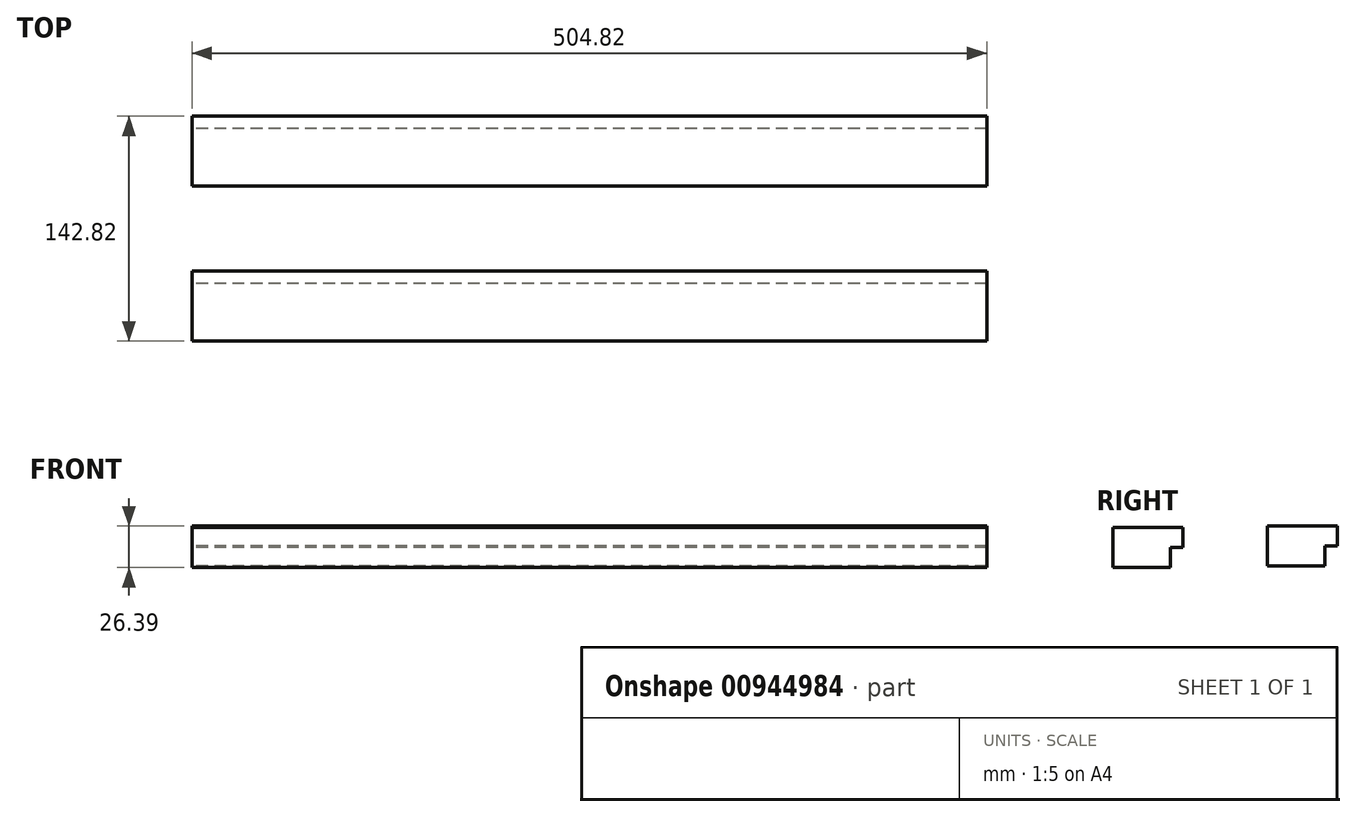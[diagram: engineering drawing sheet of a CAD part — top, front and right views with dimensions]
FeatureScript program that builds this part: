
annotation { "Feature Type Name" : "Feature", "Feature Type Description" : "" }
export const myFeature = defineFeature(function(context is Context, id is Id, definition is map)
    precondition{}
    {
        {
            var Q0;
            Q0=qCreatedBy(makeId("Right.planeOp"),FACE);
            var sketch = newSketch(context, id + "F0", { "sketchPlane" : qUnion([Q0])});
            skLineSegment(sketch, "E0.bottom", {"start": v(-98.37, 30.25) * mm, "end": v(-61.85, 30.25) * mm});
            skLineSegment(sketch, "E0.top", {"start": v(-98.37, 4.85) * mm, "end": v(-61.85, 4.85) * mm});
            skLineSegment(sketch, "E0.left", {"start": v(-98.37, 30.25) * mm, "end": v(-98.37, 4.85) * mm});
            skLineSegment(sketch, "E0.right", {"start": v(-61.85, 30.25) * mm, "end": v(-61.85, 4.85) * mm});
            skLineSegment(sketch, "E1.bottom", {"start": v(-61.85, 30.25) * mm, "end": v(-53.92, 30.25) * mm});
            skLineSegment(sketch, "E1.top", {"start": v(-61.85, 17.55) * mm, "end": v(-53.92, 17.55) * mm});
            skLineSegment(sketch, "E1.left", {"start": v(-61.85, 30.25) * mm, "end": v(-61.85, 17.55) * mm});
            skLineSegment(sketch, "E1.right", {"start": v(-53.92, 30.25) * mm, "end": v(-53.92, 17.55) * mm});
            skLineSegment(sketch, "E2.bottom", {"start": v(0, 31.24) * mm, "end": v(36.51, 31.24) * mm});
            skLineSegment(sketch, "E2.top", {"start": v(0, 5.84) * mm, "end": v(36.51, 5.84) * mm});
            skLineSegment(sketch, "E2.left", {"start": v(0, 31.24) * mm, "end": v(0, 5.84) * mm});
            skLineSegment(sketch, "E2.right", {"start": v(36.51, 31.24) * mm, "end": v(36.51, 5.84) * mm});
            skLineSegment(sketch, "E3.bottom", {"start": v(36.51, 31.24) * mm, "end": v(44.45, 31.24) * mm});
            skLineSegment(sketch, "E3.top", {"start": v(36.51, 18.54) * mm, "end": v(44.45, 18.54) * mm});
            skLineSegment(sketch, "E3.left", {"start": v(36.51, 31.24) * mm, "end": v(36.51, 18.54) * mm});
            skLineSegment(sketch, "E3.right", {"start": v(44.45, 31.24) * mm, "end": v(44.45, 18.54) * mm});
            skSolve(sketch);
        }
        {
            var Q0;
            Q0=makeQuery(id+"F0.imprint","IMPRINT",FACE,{"disambiguationData":[TD([[makeQuery(id+"F0.imprint","IMPRINT",EDGE,{"derivedFrom":sQuery(id+"F0.wireOp",EDGE,"E0.bottom")}),-1.0]])]});
            var Q1;
            Q1=makeQuery(id+"F0.imprint","IMPRINT",FACE,{"disambiguationData":[TD([[makeQuery(id+"F0.imprint","IMPRINT",EDGE,{"derivedFrom":sQuery(id+"F0.wireOp",EDGE,"E1.bottom")}),-1.0]])]});
            var Q2;
            Q2=makeQuery(id+"F0.imprint","IMPRINT",FACE,{"disambiguationData":[TD([[makeQuery(id+"F0.imprint","IMPRINT",EDGE,{"derivedFrom":sQuery(id+"F0.wireOp",EDGE,"E2.bottom")}),-1.0]])]});
            var Q3;
            Q3=makeQuery(id+"F0.imprint","IMPRINT",FACE,{"disambiguationData":[TD([[makeQuery(id+"F0.imprint","IMPRINT",EDGE,{"derivedFrom":sQuery(id+"F0.wireOp",EDGE,"E3.bottom")}),-1.0]])]});
            extrude(context, id + "F1", {"entities" : qUnion([Q0, Q1, Q2, Q3]), "depth" : 504.82 * mm, "offsetDistance" : 25.4 * mm});
        }
    });
